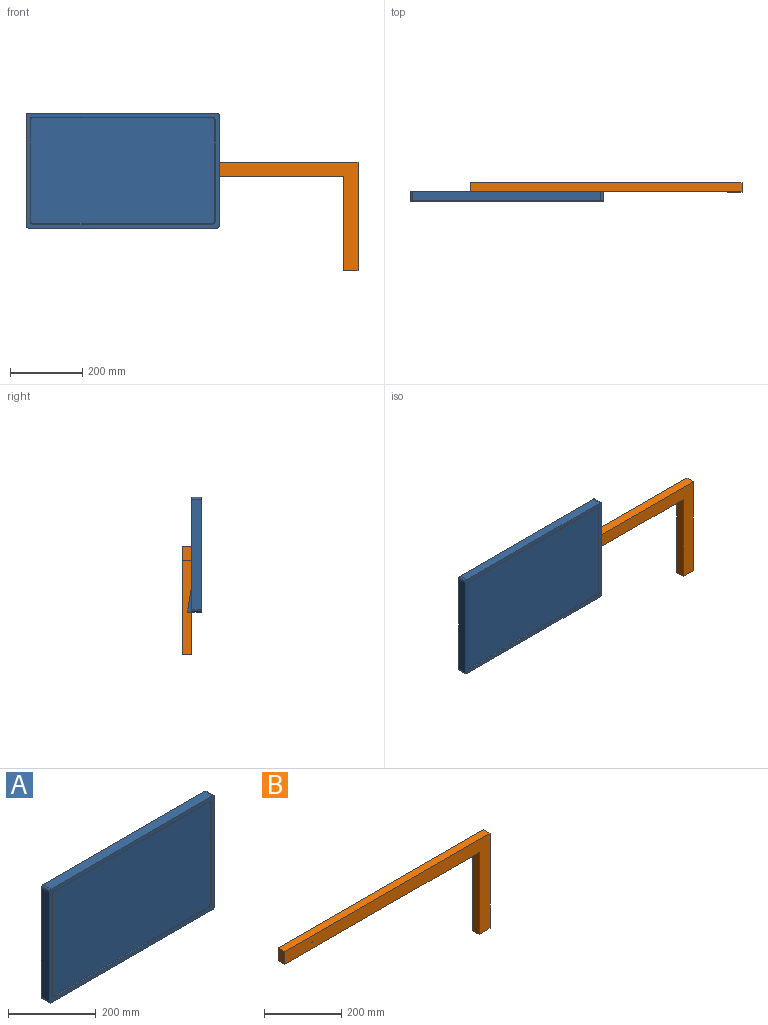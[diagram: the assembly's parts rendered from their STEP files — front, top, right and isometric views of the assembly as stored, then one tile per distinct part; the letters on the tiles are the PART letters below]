
ASSEMBLY  parts=2 mates=1
PART A: 23 faces, bbox 533.4x38.1x317.5 mm
  f0: plane 533.4x317.5mm, normal (0,1,0), area 165463.7mm2, adj f1,f2,f3,f4,f6,f7,f8,f9
  f1: plane 304.8x25.4mm, normal (-1,0,0), area 7741.9mm2, adj f0,f5,f7,f8
  f2: plane 520.72x25.42mm, normal (0,0,-1), area 13225.8mm2, adj f0,f5,f8,f9,f10
  f3: plane 304.8x25.4mm, normal (1,0,0), area 7741.9mm2, adj f0,f5,f6,f9
  f4: plane 520.7x25.4mm, normal (0,0,1), area 13225.8mm2, adj f0,f5,f6,f7
  f5: plane 533.4x317.5mm, normal (0,-1,0), area 18436.8mm2, adj f1,f2,f3,f4,f6,f7,f8,f9
  f6: cylinder r=6.35mm len=25.4mm, axis (0,1,0), area 253.4mm2, adj f0,f3,f4,f5
  f7: cylinder r=6.35mm len=25.4mm, axis (0,-1,0), area 253.4mm2, adj f0,f1,f4,f5
  f8: cylinder r=6.35mm len=25.4mm, axis (0,1,0), area 253.4mm2, adj f0,f1,f2,f5
  f9: cylinder r=6.35mm len=25.4mm, axis (0,-1,0), area 253.4mm2, adj f0,f2,f3,f5
  f10: plane 50.82x12.7mm, normal (0,0,-1), area 644.3mm2, adj f2,f11,f12,f13
  f11: plane 75.91x50.8mm, normal (0,0.99,0.16), area 3909.4mm2, adj f0,f10,f12,f13
  f12: plane 75.91x12.68mm, normal (1,0,0), area 481.3mm2, adj f0,f10,f11
  f13: plane 75.91x12.68mm, normal (-1,0,0), area 481.3mm2, adj f0,f10,f11
  f14: plane 508x292.1mm, normal (0,-1,0), area 148352.2mm2, adj f15,f16,f17,f18,f19,f20,f21,f22
  f15: plane 279.4x1.59mm, normal (0.71,-0.71,0), area 627.3mm2, adj f5,f14,f16,f17
  f16: cone r=6.35mm half-angle=45deg, axis (0,-1,0), area 25.2mm2, adj f5,f14,f15,f18
  f17: cone r=6.35mm half-angle=45deg, axis (0,-1,0), area 25.2mm2, adj f5,f14,f15,f19
  f18: plane 495.3x1.59mm, normal (0,-0.71,0.71), area 1112mm2, adj f5,f14,f16,f20
  f19: plane 495.3x1.59mm, normal (0,-0.71,-0.71), area 1112mm2, adj f5,f14,f17,f21
  f20: cone r=6.35mm half-angle=45deg, axis (0,-1,0), area 25.2mm2, adj f5,f14,f18,f22
  f21: cone r=6.35mm half-angle=45deg, axis (0,-1,0), area 25.2mm2, adj f5,f14,f19,f22
  f22: plane 279.4x1.59mm, normal (-0.71,-0.71,0), area 627.3mm2, adj f5,f14,f20,f21
PART B: 9 faces, bbox 750x25x300 mm
  f0: plane 710x25mm, normal (0,0,-1), area 17750mm2, adj f1,f6,f7,f8
  f1: plane 260x25mm, normal (-1,0,0), area 6500mm2, adj f0,f2,f7,f8
  f2: plane 40x25mm, normal (0,0,-1), area 1000mm2, adj f1,f3,f7,f8
  f3: plane 300x25mm, normal (1,0,0), area 7500mm2, adj f2,f4,f7,f8
  f4: plane 750x25mm, normal (0,0,1), area 18750mm2, adj f3,f6,f7,f8
  f5: cylinder r=1.5mm len=25mm, axis (0,1,0), area 235.6mm2, adj f7,f8
  f6: plane 40x25mm, normal (-1,0,0), area 1000mm2, adj f0,f4,f7,f8
  f7: plane 750x300mm, normal (0,-1,0), area 40392.9mm2, adj f0,f1,f2,f3,f4,f5,f6
  f8: plane 750x300mm, normal (0,1,0), area 40392.9mm2, adj f0,f1,f2,f3,f4,f5,f6
PLACE A t=(-13.21,24.49,44.83)mm
PLACE B t=(-21.36,49.49,-32.51)mm
MATE fastened A.f0 <-> B.f5  axis (0,1,0) through (-12.2,24.49,34.45)mm
